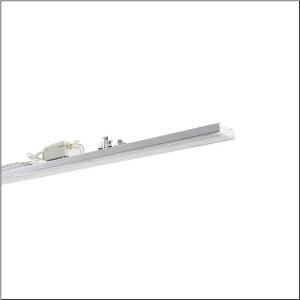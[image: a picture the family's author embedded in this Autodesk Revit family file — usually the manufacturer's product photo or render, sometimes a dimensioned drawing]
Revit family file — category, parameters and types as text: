
# Revit family: licross_21_recessed_ho_52te1edn4e5s
name_source: partatom
category: Lighting Fixtures
units: mm (PartAtom-declared; Revit-internal decimal feet)

## family parameters
Cut with Voids When Loaded = No
Host = Face
Light Source = No
Part Type = Normal
Room Calculation Point = No
Round Connector Dimension = Use Diameter
Shared = No

## types (1)
- --- (1 x LED, 14620 lm, 84.6 W, 4000K)
    Apparent Load = 85 VA
    CIE Flux Codes = 85 95 99 100 100
    Color Rendering = 80
    Color Temperature = 4000K
    Default Elevation = 1800 mm
    Description = Licross 21 Recessed HO, luminaire insert, of sheet steel, galvanised, coil coated, white, length: 1.500mm, width: 66mm, height: 67mm, LED rated luminous flux: 14.620lm, light colour: 840, SDCM (Standard Deviation of Colour Matching)MacAdam ≤ 3 SDCM (initial), control gear: DALI 2, with plug, 5-pole, with phase selection, mains connection: 220..240V, AC, 50/60Hz, rated input power: 85W, internal wiring halogen-free, primary light control with lens, of plastic, primary optical cover: cover, of PMMA, light emission: direct distribution, primary light characteristic: symmetric, protection rating (complete): IP54, insulation class (complete): insulation class I (protective earthing), certification: CE, ENEC, VDE, UKCA, protection symbol: D if used in an environment with non-conductive dust loads with corresponding accessories, impact resistance: IK06, permissible ambient temperature for indoor applications: -25..+30°C, corresponds to IFS (International Featured Standards) requirements for safety and quality in the food industry, reducing of maximum allowable ambient temperature of 5°C with ceiling mounting, LABS conformity tested according to VDMA 24364:2018-05, The light source and the operating device comply with the requirements of the Ecodesign Regulation (EU) 2019/2020 and are replaceable in accordance with this regulation, packaging unit: 1 piece
    Height = 58 mm
    Lamp = 1 x LED
    Lamp Light Flux = 14620 lm
    Lamp Power = 84.6 W
    Lamp count = 1
    Length = 1500 mm
    Luminous efficacy = 173 lm/W
    Manufacturer = Siteco
    ModVariant = No
    Model = 52TE1EDN4E5S
    Mounting Place = Ceiling
    Mounting Type = Pendant
    Number of Poles = 1
    OnlyDefault = Yes
    Power Factor = 1
    Product Name = Licross 21 Recessed HO
    Product group = luminaire insert | ceiling pendant
    ProductGroupID = 901
    Protection Class = Protection class I
    Protection Degree = IP 54
    RLX_Detail_Level = 1
    RLX_Emergency_Light_Flux = 0 lm
    RLX_Emergency_Type = 0
    RLX_Emergency_Type_DB = No
    RlxData = <blob elided: 25021 chars, md5=0bb4fd4e>
    Socket = socket
    Standby Power = 0 W
    System Light Flux = 14620 lm
    System Power = 85 W
    Type Comments = factory setting: luminous flux: 100 % | dim-lin: 254 | 484 mA
    Type Image = l_1296930.jpg
    URL = http://relux.com
    VarID = @adj_126777
    Voltage = 0 V
    Weight = 0.00 kg
    Width = 66 mm

## geometry (parser evidence)
native form markers: Blend x4, Sweep x12
no freeform markers — native parametric forms only
